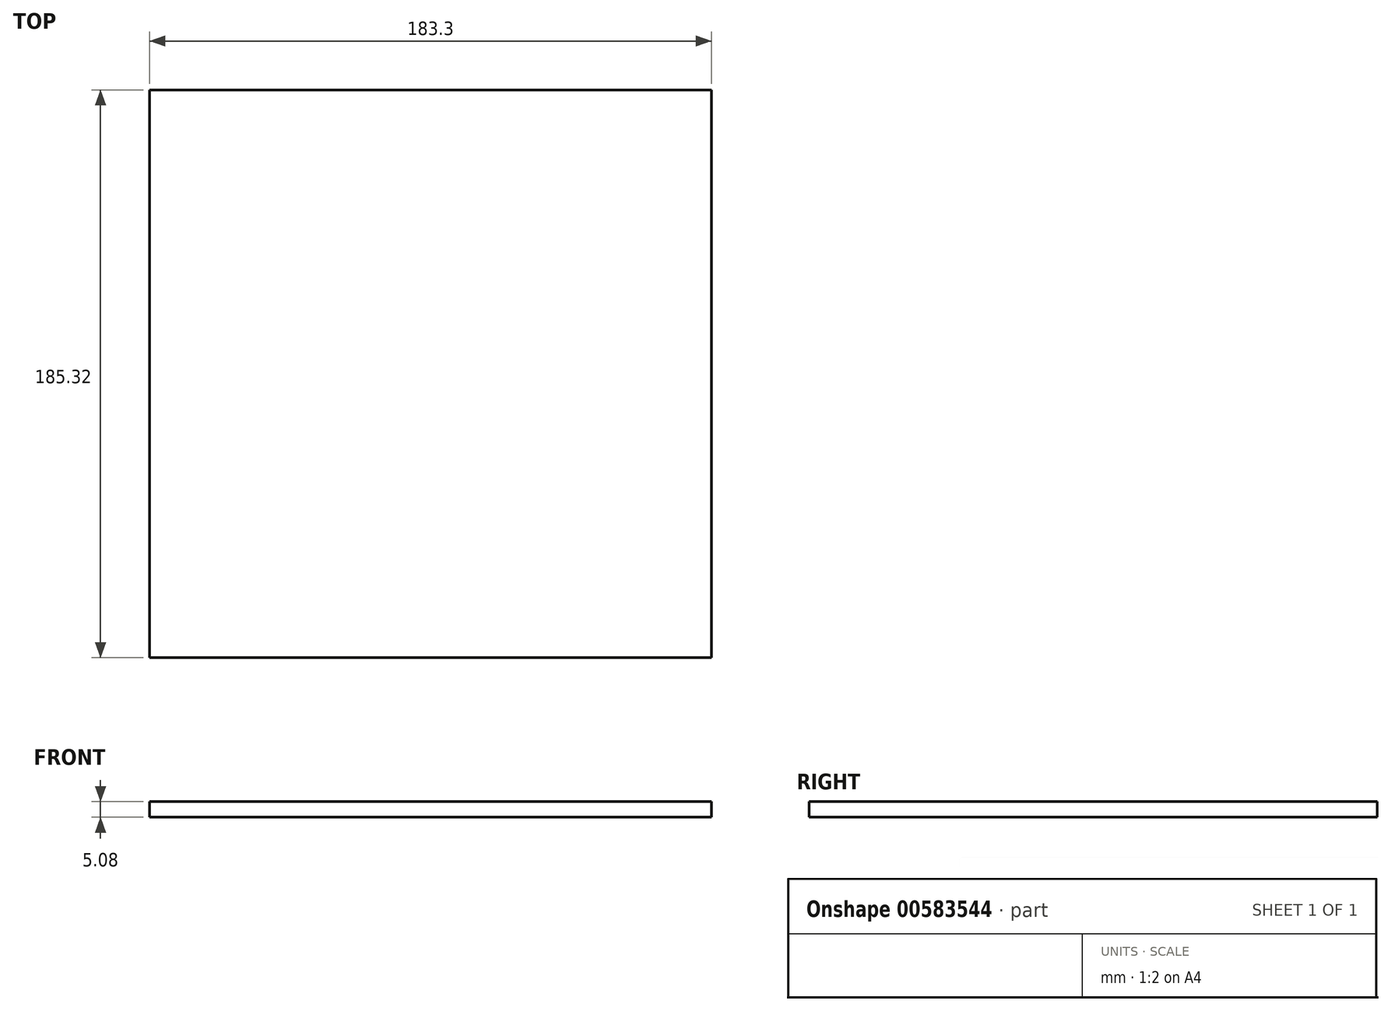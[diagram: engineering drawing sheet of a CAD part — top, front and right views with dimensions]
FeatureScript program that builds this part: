
annotation { "Feature Type Name" : "Feature", "Feature Type Description" : "" }
export const myFeature = defineFeature(function(context is Context, id is Id, definition is map)
    precondition{}
    {
        {
            var Q0;
            Q0=qCreatedBy(makeId("Top.planeOp"),FACE);
            var sketch = newSketch(context, id + "F0", { "sketchPlane" : qUnion([Q0])});
            skLineSegment(sketch, "E0.bottom", {"start": v(0, 0) * mm, "end": v(0, 0) * mm});
            skLineSegment(sketch, "E0.top", {"start": v(0, 0) * mm, "end": v(0, 0) * mm});
            skLineSegment(sketch, "E0.left", {"start": v(0, 0) * mm, "end": v(0, 0) * mm});
            skLineSegment(sketch, "E0.right", {"start": v(0, 0) * mm, "end": v(0, 0) * mm});
            skPoint(sketch, "E0.middle", {"position": v(0, 0) * mm});
            skLineSegment(sketch, "E1.bottom", {"start": v(91.65, -92.66) * mm, "end": v(-91.65, -92.66) * mm});
            skLineSegment(sketch, "E1.top", {"start": v(91.65, 92.66) * mm, "end": v(-91.65, 92.66) * mm});
            skLineSegment(sketch, "E1.left", {"start": v(91.65, -92.66) * mm, "end": v(91.65, 92.66) * mm});
            skLineSegment(sketch, "E1.right", {"start": v(-91.65, -92.66) * mm, "end": v(-91.65, 92.66) * mm});
            skSolve(sketch);
        }
        {
            var Q0;
            Q0 = qSketchRegion(id + "F0", true);
            extrude(context, id + "F1", {"entities" : qUnion([Q0]), "depth" : 5.08 * mm, "offsetDistance" : 25.4 * mm});
        }
    });
